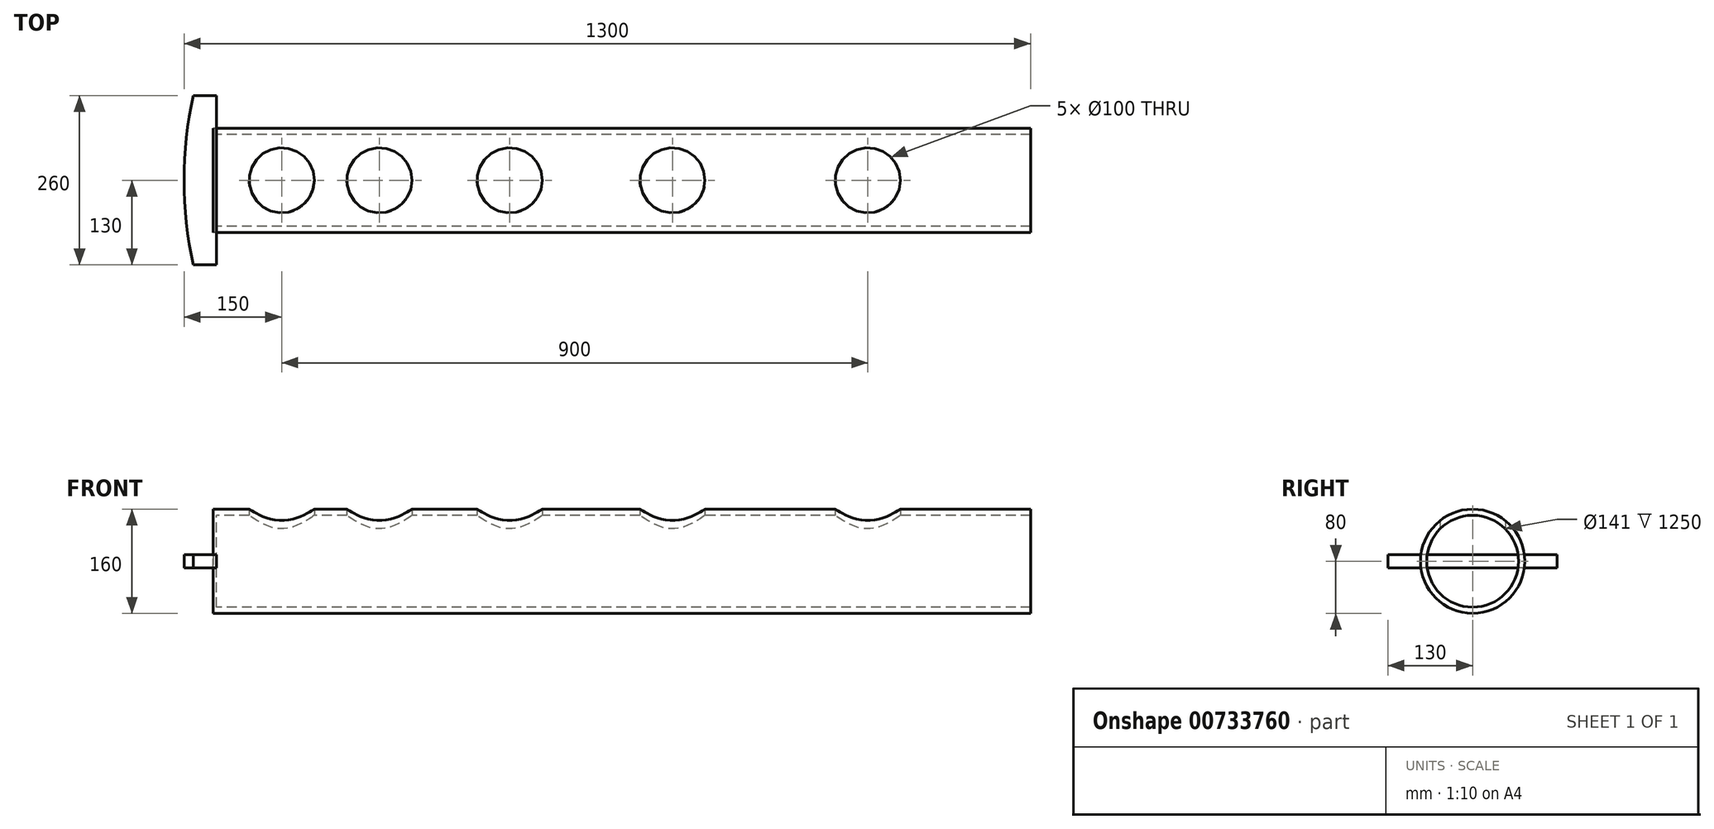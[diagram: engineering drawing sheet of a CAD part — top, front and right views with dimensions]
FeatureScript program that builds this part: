
annotation { "Feature Type Name" : "Feature", "Feature Type Description" : "" }
export const myFeature = defineFeature(function(context is Context, id is Id, definition is map)
    precondition{}
    {
        {
            var Q0;
            Q0=qCreatedBy(makeId("Right.planeOp"),FACE);
            var sketch = newSketch(context, id + "F0", { "sketchPlane" : qUnion([Q0])});
            skCircle(sketch, "E0", {"center": v(0, 0) * mm, "radius": 80 * mm});
            skCircle(sketch, "E1", {"center": v(0, 0) * mm, "radius": 70.5 * mm});
            skSolve(sketch);
        }
        {
            var Q0;
            Q0=qSketchRegion(id+"F0",true);
            extrude(context, id + "F1", {"entities" : qUnion([Q0]), "depth" : 1250 * mm, "offsetDistance" : 25 * mm});
        }
        {
            var Q0;
            Q0=makeQuery(id+"F1.opExtrude","CAP_FACE",FACE,{"disambiguationData":[OSD([sQuery(id+"F0.wireOp",EDGE,"E0"),sQuery(id+"F0.wireOp",EDGE,"E1")])],"isStart":true});
            var sketch = newSketch(context, id + "F2", { "sketchPlane" : qUnion([Q0])});
            skCircle(sketch, "E2", {"center": v(0, 0) * mm, "radius": 80 * mm});
            skSolve(sketch);
        }
        {
            var Q0;
            Q0=qSketchRegion(id+"F2",true);
            extrude(context, id + "F3", {"entities" : qUnion([Q0]), "operationType" : NewBodyOperationType.ADD, "depth" : 5 * mm, "offsetDistance" : 25 * mm});
        }
        {
            var Q0;
            Q0=qCreatedBy(makeId("Top.planeOp"),FACE);
            var sketch = newSketch(context, id + "F4", { "sketchPlane" : qUnion([Q0])});
            skLineSegment(sketch, "E3", {"start": v(0, 0) * mm, "end": v(1100, 0) * mm});
            skLineSegment(sketch, "E4", {"start": v(1100, 0) * mm, "end": v(1151.8, -193.18) * mm});
            skLineSegment(sketch, "E5", {"start": v(0, 0) * mm, "end": v(100, 0) * mm});
            skCircle(sketch, "E6", {"center": v(100, 0) * mm, "radius": 50 * mm});
            skLineSegment(sketch, "E7", {"start": v(100, 0) * mm, "end": v(250, 0) * mm});
            skLineSegment(sketch, "E8", {"start": v(250, 0) * mm, "end": v(450, 0) * mm});
            skLineSegment(sketch, "E9", {"start": v(450, 0) * mm, "end": v(700, 0) * mm});
            skLineSegment(sketch, "E10", {"start": v(700, 0) * mm, "end": v(1000, 0) * mm});
            skCircle(sketch, "E11", {"center": v(250, 0) * mm, "radius": 50 * mm});
            skCircle(sketch, "E12", {"center": v(450, 0) * mm, "radius": 50 * mm});
            skCircle(sketch, "E13", {"center": v(700, 0) * mm, "radius": 50 * mm});
            skCircle(sketch, "E14", {"center": v(1000, 0) * mm, "radius": 50 * mm});
            skPoint(sketch, "E15.middle", {"position": v(0, 0) * mm});
            skLineSegment(sketch, "E16", {"start": v(0, 0) * mm, "end": v(0, 130) * mm});
            skLineSegment(sketch, "E17", {"start": v(0, 0) * mm, "end": v(0, -130) * mm});
            skPoint(sketch, "E18.orphan", {"position": v(75, -130) * mm});
            skPoint(sketch, "E19.orphan", {"position": v(75, 130) * mm});
            skArc(sketch, "E20", {"start": v(-35.75, 130) * mm, "mid": v(-50, 0) * mm, "end": v(-35.75, -130) * mm});
            skLineSegment(sketch, "E21", {"start": v(-35.75, 130) * mm, "end": v(0, 130) * mm});
            skLineSegment(sketch, "E22", {"start": v(0, -130) * mm, "end": v(-35.75, -130) * mm});
            skSolve(sketch);
        }
        {
            var Q0;
            {var subQ0=sQuery(id+"F4.wireOp",EDGE,"E7");var subQ1=sQuery(id+"F4.wireOp",EDGE,"E5");var subQ2=makeQuery(id+"F4.imprint","INTERSECT",VERTEX,{"derivedFrom":[subQ1,subQ0]});Q0=makeQuery(id+"F4.imprint","IMPRINT",FACE,{"disambiguationData":[TD([[makeQuery(id+"F4.imprint","IMPRINT",EDGE,{"disambiguationData":[TD([[subQ2,1.0]])],"derivedFrom":subQ1}),-1.0]])]});}
            var Q1;
            {var subQ0=sQuery(id+"F4.wireOp",EDGE,"E7");var subQ1=sQuery(id+"F4.wireOp",EDGE,"E5");var subQ2=makeQuery(id+"F4.imprint","INTERSECT",VERTEX,{"derivedFrom":[subQ1,subQ0]});Q1=makeQuery(id+"F4.imprint","IMPRINT",FACE,{"disambiguationData":[TD([[makeQuery(id+"F4.imprint","IMPRINT",EDGE,{"disambiguationData":[TD([[subQ2,1.0]])],"derivedFrom":subQ1}),1.0]])]});}
            var Q2;
            {var subQ0=sQuery(id+"F4.wireOp",EDGE,"E8");var subQ1=sQuery(id+"F4.wireOp",EDGE,"E7");var subQ2=makeQuery(id+"F4.imprint","INTERSECT",VERTEX,{"derivedFrom":[subQ1,subQ0]});Q2=makeQuery(id+"F4.imprint","IMPRINT",FACE,{"disambiguationData":[TD([[makeQuery(id+"F4.imprint","IMPRINT",EDGE,{"disambiguationData":[TD([[subQ2,1.0]])],"derivedFrom":subQ1}),1.0]])]});}
            var Q3;
            {var subQ0=sQuery(id+"F4.wireOp",EDGE,"E8");var subQ1=sQuery(id+"F4.wireOp",EDGE,"E7");var subQ2=makeQuery(id+"F4.imprint","INTERSECT",VERTEX,{"derivedFrom":[subQ1,subQ0]});Q3=makeQuery(id+"F4.imprint","IMPRINT",FACE,{"disambiguationData":[TD([[makeQuery(id+"F4.imprint","IMPRINT",EDGE,{"disambiguationData":[TD([[subQ2,1.0]])],"derivedFrom":subQ1}),-1.0]])]});}
            var Q4;
            {var subQ0=sQuery(id+"F4.wireOp",EDGE,"E9");var subQ1=sQuery(id+"F4.wireOp",EDGE,"E8");var subQ2=makeQuery(id+"F4.imprint","INTERSECT",VERTEX,{"derivedFrom":[subQ1,subQ0]});Q4=makeQuery(id+"F4.imprint","IMPRINT",FACE,{"disambiguationData":[TD([[makeQuery(id+"F4.imprint","IMPRINT",EDGE,{"disambiguationData":[TD([[subQ2,1.0]])],"derivedFrom":subQ1}),1.0]])]});}
            var Q5;
            {var subQ0=sQuery(id+"F4.wireOp",EDGE,"E9");var subQ1=sQuery(id+"F4.wireOp",EDGE,"E8");var subQ2=makeQuery(id+"F4.imprint","INTERSECT",VERTEX,{"derivedFrom":[subQ1,subQ0]});Q5=makeQuery(id+"F4.imprint","IMPRINT",FACE,{"disambiguationData":[TD([[makeQuery(id+"F4.imprint","IMPRINT",EDGE,{"disambiguationData":[TD([[subQ2,1.0]])],"derivedFrom":subQ1}),-1.0]])]});}
            var Q6;
            {var subQ0=sQuery(id+"F4.wireOp",EDGE,"E10");var subQ1=sQuery(id+"F4.wireOp",EDGE,"E9");var subQ2=makeQuery(id+"F4.imprint","INTERSECT",VERTEX,{"derivedFrom":[subQ1,subQ0]});Q6=makeQuery(id+"F4.imprint","IMPRINT",FACE,{"disambiguationData":[TD([[makeQuery(id+"F4.imprint","IMPRINT",EDGE,{"disambiguationData":[TD([[subQ2,1.0]])],"derivedFrom":subQ1}),1.0]])]});}
            var Q7;
            {var subQ0=sQuery(id+"F4.wireOp",EDGE,"E10");var subQ1=sQuery(id+"F4.wireOp",EDGE,"E9");var subQ2=makeQuery(id+"F4.imprint","INTERSECT",VERTEX,{"derivedFrom":[subQ1,subQ0]});Q7=makeQuery(id+"F4.imprint","IMPRINT",FACE,{"disambiguationData":[TD([[makeQuery(id+"F4.imprint","IMPRINT",EDGE,{"disambiguationData":[TD([[subQ2,1.0]])],"derivedFrom":subQ1}),-1.0]])]});}
            var Q8;
            {var subQ0=sQuery(id+"F4.wireOp",EDGE,"E10");var subQ1=sQuery(id+"F4.wireOp",EDGE,"E3");var subQ2=makeQuery(id+"F4.imprint","INTERSECT",VERTEX,{"derivedFrom":[subQ1,subQ0]});Q8=makeQuery(id+"F4.imprint","IMPRINT",FACE,{"disambiguationData":[TD([[makeQuery(id+"F4.imprint","IMPRINT",EDGE,{"disambiguationData":[TD([[subQ2,-1.0]])],"derivedFrom":subQ1}),1.0]])]});}
            var Q9;
            {var subQ0=sQuery(id+"F4.wireOp",EDGE,"E10");var subQ1=sQuery(id+"F4.wireOp",EDGE,"E3");var subQ2=makeQuery(id+"F4.imprint","INTERSECT",VERTEX,{"derivedFrom":[subQ1,subQ0]});Q9=makeQuery(id+"F4.imprint","IMPRINT",FACE,{"disambiguationData":[TD([[makeQuery(id+"F4.imprint","IMPRINT",EDGE,{"disambiguationData":[TD([[subQ2,-1.0]])],"derivedFrom":subQ1}),-1.0]])]});}
            extrude(context, id + "F5", {"entities" : qUnion([Q0, Q1, Q2, Q3, Q4, Q5, Q6, Q7, Q8, Q9]), "operationType" : NewBodyOperationType.REMOVE, "depth" : 200 * mm, "offsetDistance" : 25 * mm});
        }
        {
            var Q0;
            Q0=makeQuery(id+"F4.imprint","IMPRINT",FACE,{"disambiguationData":[TD([[makeQuery(id+"F4.imprint","IMPRINT",EDGE,{"derivedFrom":sQuery(id+"F4.wireOp",EDGE,"E16")}),1.0]])]});
            extrude(context, id + "F6", {"entities" : qUnion([Q0]), "endBound" : BoundingType.SYMMETRIC, "oppositeDirection" : true, "depth" : 20 * mm, "offsetDistance" : 25 * mm});
        }
    });
